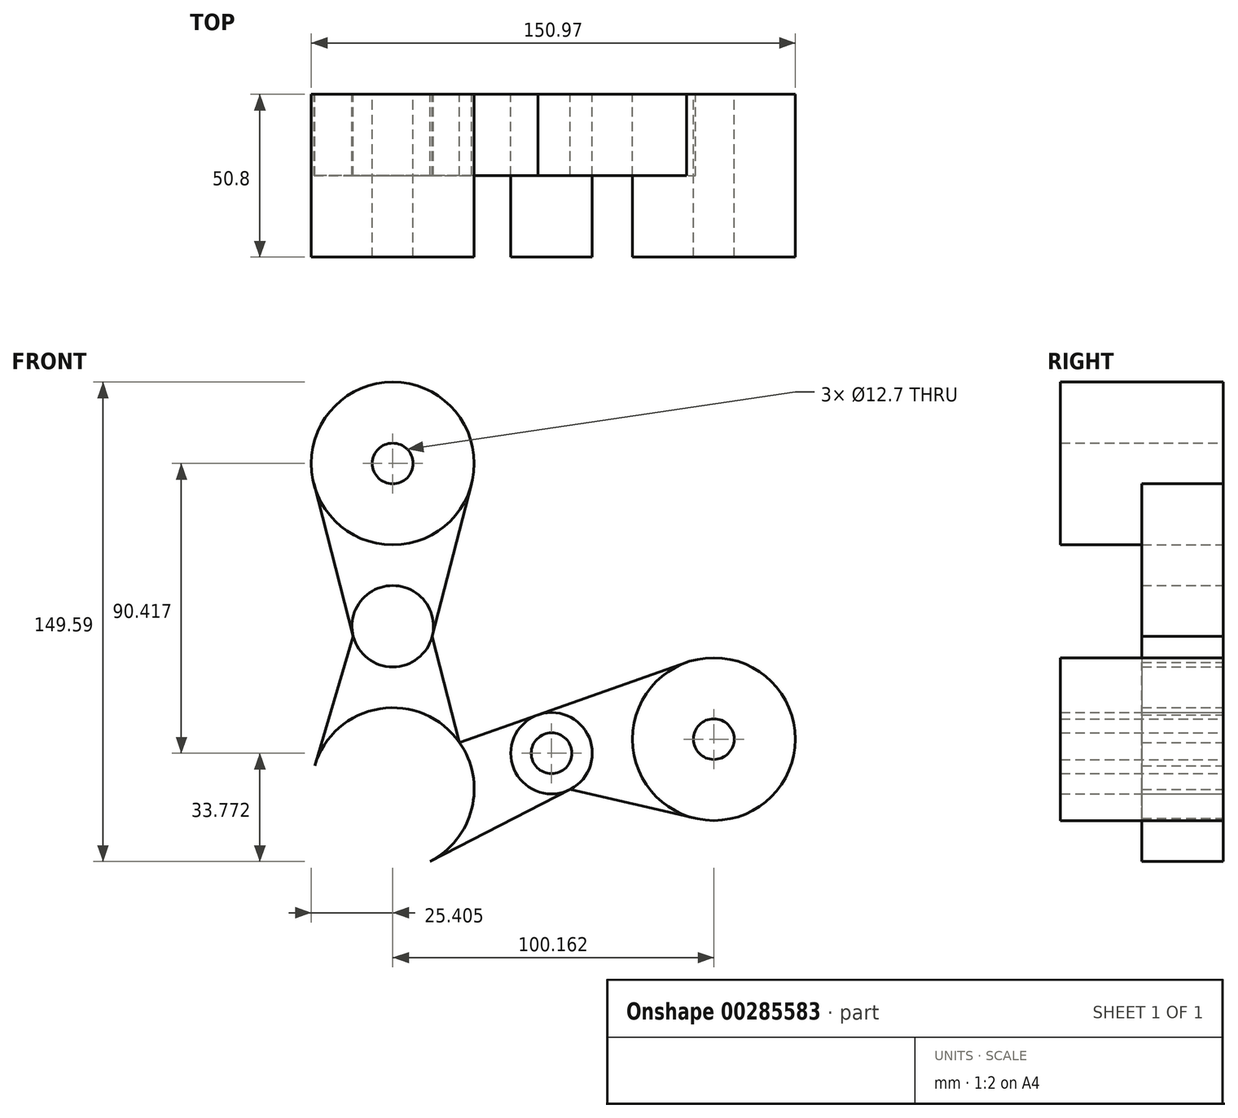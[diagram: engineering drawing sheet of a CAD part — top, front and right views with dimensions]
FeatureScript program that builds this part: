
annotation { "Feature Type Name" : "Feature", "Feature Type Description" : "" }
export const myFeature = defineFeature(function(context is Context, id is Id, definition is map)
    precondition{}
    {
        {
            var Q0;
            Q0=qCreatedBy(makeId("Front.planeOp"),FACE);
            var sketch = newSketch(context, id + "F0", { "sketchPlane" : qUnion([Q0])});
            skLineSegment(sketch, "E0", {"start": v(-250.7, 15.24) * mm, "end": v(-250.7, -86.36) * mm});
            skCircle(sketch, "E1", {"center": v(-250.7, 15.24) * mm, "radius": 25.4 * mm});
            skLineSegment(sketch, "E2", {"start": v(-250.7, 15.24) * mm, "end": v(-250.7, -35.56) * mm});
            skLineSegment(sketch, "E3", {"start": v(-250.7, -35.56) * mm, "end": v(-250.7, -86.36) * mm});
            skLineSegment(sketch, "E4", {"start": v(-201.15, -75.18) * mm, "end": v(-250.7, -86.36) * mm});
            skCircle(sketch, "E5", {"center": v(-250.7, -86.36) * mm, "radius": 25.4 * mm});
            skCircle(sketch, "E6", {"center": v(-150.54, -70.77) * mm, "radius": 25.4 * mm});
            skLineSegment(sketch, "E7", {"start": v(-201.15, -75.18) * mm, "end": v(-150.54, -70.77) * mm});
            skCircle(sketch, "E8", {"center": v(-250.7, -35.56) * mm, "radius": 12.7 * mm});
            skCircle(sketch, "E9", {"center": v(-201.15, -75.18) * mm, "radius": 12.7 * mm});
            skLineSegment(sketch, "E10", {"start": v(-275.3, 8.89) * mm, "end": v(-263, -38.74) * mm});
            skLineSegment(sketch, "E11", {"start": v(-263, -38.74) * mm, "end": v(-275.04, -79.1) * mm});
            skLineSegment(sketch, "E12", {"start": v(-226.11, 8.89) * mm, "end": v(-238.4, -38.74) * mm});
            skLineSegment(sketch, "E13", {"start": v(-205.38, -63.2) * mm, "end": v(-159, -46.82) * mm});
            skLineSegment(sketch, "E14", {"start": v(-238.4, -38.74) * mm, "end": v(-229.86, -71.85) * mm});
            skLineSegment(sketch, "E15", {"start": v(-229.86, -71.85) * mm, "end": v(-205.38, -63.2) * mm});
            skLineSegment(sketch, "E16", {"start": v(-195.35, -86.47) * mm, "end": v(-156.27, -95.52) * mm});
            skLineSegment(sketch, "E17", {"start": v(-239.1, -108.95) * mm, "end": v(-195.35, -86.47) * mm});
            skSolve(sketch);
        }
        {
            var Q0;
            {var subQ0=sQuery(id+"F0.wireOp",EDGE,"E1");var subQ1=makeQuery(id+"F0.imprint","INTERSECT",VERTEX,{"derivedFrom":[subQ0,sQuery(id+"F0.wireOp",EDGE,"E10")]});Q0=makeQuery(id+"F0.imprint","IMPRINT",FACE,{"disambiguationData":[TD([[makeQuery(id+"F0.imprint","IMPRINT",EDGE,{"disambiguationData":[TD([[subQ1,-1.0]])],"derivedFrom":subQ0}),1.0]])]});}
            var Q1;
            {var subQ0=sQuery(id+"F0.wireOp",EDGE,"E3");var subQ1=sQuery(id+"F0.wireOp",EDGE,"E2");var subQ2=makeQuery(id+"F0.imprint","INTERSECT",VERTEX,{"derivedFrom":[subQ1,subQ0]});Q1=makeQuery(id+"F0.imprint","IMPRINT",FACE,{"disambiguationData":[TD([[makeQuery(id+"F0.imprint","IMPRINT",EDGE,{"disambiguationData":[TD([[subQ2,1.0]])],"derivedFrom":subQ1}),1.0]])]});}
            var Q2;
            {var subQ0=sQuery(id+"F0.wireOp",EDGE,"E3");var subQ1=sQuery(id+"F0.wireOp",EDGE,"E2");var subQ2=makeQuery(id+"F0.imprint","INTERSECT",VERTEX,{"derivedFrom":[subQ1,subQ0]});Q2=makeQuery(id+"F0.imprint","IMPRINT",FACE,{"disambiguationData":[TD([[makeQuery(id+"F0.imprint","IMPRINT",EDGE,{"disambiguationData":[TD([[subQ2,1.0]])],"derivedFrom":subQ1}),-1.0]])]});}
            var Q3;
            {var subQ3=sQuery(id+"F0.wireOp",EDGE,"E3");var subQ5=sQuery(id+"F0.wireOp",EDGE,"E4");var subQ6=makeQuery(id+"F0.imprint","INTERSECT",VERTEX,{"derivedFrom":[subQ3,subQ5]});Q3=makeQuery(id+"F0.imprint","IMPRINT",FACE,{"disambiguationData":[TD([[makeQuery(id+"F0.imprint","IMPRINT",EDGE,{"disambiguationData":[TD([[subQ6,1.0]])],"derivedFrom":subQ3}),-1.0]])]});}
            var Q4;
            {var subQ0=sQuery(id+"F0.wireOp",EDGE,"E4");var subQ1=sQuery(id+"F0.wireOp",EDGE,"E3");var subQ2=makeQuery(id+"F0.imprint","INTERSECT",VERTEX,{"derivedFrom":[subQ1,subQ0]});Q4=makeQuery(id+"F0.imprint","IMPRINT",FACE,{"disambiguationData":[TD([[makeQuery(id+"F0.imprint","IMPRINT",EDGE,{"disambiguationData":[TD([[subQ2,1.0]])],"derivedFrom":subQ1}),1.0]])]});}
            var Q5;
            {var subQ0=sQuery(id+"F0.wireOp",EDGE,"E7");var subQ1=sQuery(id+"F0.wireOp",EDGE,"E4");var subQ2=makeQuery(id+"F0.imprint","INTERSECT",VERTEX,{"derivedFrom":[subQ1,subQ0]});Q5=makeQuery(id+"F0.imprint","IMPRINT",FACE,{"disambiguationData":[TD([[makeQuery(id+"F0.imprint","IMPRINT",EDGE,{"disambiguationData":[TD([[subQ2,-1.0]])],"derivedFrom":subQ1}),-1.0]])]});}
            var Q6;
            {var subQ0=sQuery(id+"F0.wireOp",EDGE,"E7");var subQ1=sQuery(id+"F0.wireOp",EDGE,"E4");var subQ2=makeQuery(id+"F0.imprint","INTERSECT",VERTEX,{"derivedFrom":[subQ1,subQ0]});Q6=makeQuery(id+"F0.imprint","IMPRINT",FACE,{"disambiguationData":[TD([[makeQuery(id+"F0.imprint","IMPRINT",EDGE,{"disambiguationData":[TD([[subQ2,-1.0]])],"derivedFrom":subQ1}),1.0]])]});}
            var Q7;
            {var subQ0=sQuery(id+"F0.wireOp",EDGE,"E6");var subQ1=makeQuery(id+"F0.imprint","INTERSECT",VERTEX,{"derivedFrom":[subQ0,sQuery(id+"F0.wireOp",EDGE,"E13")]});Q7=makeQuery(id+"F0.imprint","IMPRINT",FACE,{"disambiguationData":[TD([[makeQuery(id+"F0.imprint","IMPRINT",EDGE,{"disambiguationData":[TD([[subQ1,-1.0]])],"derivedFrom":subQ0}),1.0]])]});}
            extrude(context, id + "F1", {"entities" : qUnion([Q0, Q1, Q2, Q3, Q4, Q5, Q6, Q7]), "depth" : 50.8 * mm});
        }
        {
            var Q0;
            {var subQ0=sQuery(id+"F0.wireOp",EDGE,"E10");Q0=makeQuery(id+"F0.imprint","IMPRINT",FACE,{"disambiguationData":[TD([[makeQuery(id+"F0.imprint","IMPRINT",EDGE,{"derivedFrom":subQ0}),1.0]])]});}
            var Q1;
            {var subQ0=sQuery(id+"F0.wireOp",EDGE,"E12");Q1=makeQuery(id+"F0.imprint","IMPRINT",FACE,{"disambiguationData":[TD([[makeQuery(id+"F0.imprint","IMPRINT",EDGE,{"derivedFrom":subQ0}),-1.0]])]});}
            var Q2;
            {var subQ5=sQuery(id+"F0.wireOp",EDGE,"E14");Q2=makeQuery(id+"F0.imprint","IMPRINT",FACE,{"disambiguationData":[TD([[makeQuery(id+"F0.imprint","IMPRINT",EDGE,{"derivedFrom":subQ5}),-1.0]])]});}
            var Q3;
            {var subQ5=sQuery(id+"F0.wireOp",EDGE,"E11");Q3=makeQuery(id+"F0.imprint","IMPRINT",FACE,{"disambiguationData":[TD([[makeQuery(id+"F0.imprint","IMPRINT",EDGE,{"derivedFrom":subQ5}),1.0]])]});}
            var Q4;
            {var subQ0=sQuery(id+"F0.wireOp",EDGE,"E13");Q4=makeQuery(id+"F0.imprint","IMPRINT",FACE,{"disambiguationData":[TD([[makeQuery(id+"F0.imprint","IMPRINT",EDGE,{"derivedFrom":subQ0}),-1.0]])]});}
            var Q5;
            {var subQ0=sQuery(id+"F0.wireOp",EDGE,"E16");Q5=makeQuery(id+"F0.imprint","IMPRINT",FACE,{"disambiguationData":[TD([[makeQuery(id+"F0.imprint","IMPRINT",EDGE,{"derivedFrom":subQ0}),1.0]])]});}
            var Q6;
            {var subQ5=sQuery(id+"F0.wireOp",EDGE,"E17");Q6=makeQuery(id+"F0.imprint","IMPRINT",FACE,{"disambiguationData":[TD([[makeQuery(id+"F0.imprint","IMPRINT",EDGE,{"derivedFrom":subQ5}),1.0]])]});}
            var Q7;
            {var subQ5=sQuery(id+"F0.wireOp",EDGE,"E15");Q7=makeQuery(id+"F0.imprint","IMPRINT",FACE,{"disambiguationData":[TD([[makeQuery(id+"F0.imprint","IMPRINT",EDGE,{"derivedFrom":subQ5}),-1.0]])]});}
            extrude(context, id + "F2", {"entities" : qUnion([Q0, Q1, Q2, Q3, Q4, Q5, Q6, Q7]), "depth" : 25.4 * mm});
        }
        {
            var Q0;
            Q0=sQuery(id+"F0.wireOp",VERTEX,"E0.start");
            var Q1;
            Q1=sQuery(id+"F0.wireOp",VERTEX,"E3.start");
            var Q2;
            Q2=sQuery(id+"F0.wireOp",VERTEX,"E5.center");
            var Q3;
            Q3=sQuery(id+"F0.wireOp",VERTEX,"E9.center");
            var Q4;
            Q4=sQuery(id+"F0.wireOp",VERTEX,"E7.end");
            var Q5;
            Q5=makeQuery(id+"F1.opExtrude","SWEPT_BODY",BODY,{"disambiguationData":[OSD([sQuery(id+"F0.wireOp",EDGE,"E1")])]});
            var Q6;
            Q6=makeQuery(id+"F1.opExtrude","SWEPT_BODY",BODY,{"disambiguationData":[OSD([sQuery(id+"F0.wireOp",EDGE,"E8")])]});
            var Q7;
            Q7=makeQuery(id+"F1.opExtrude","SWEPT_BODY",BODY,{"disambiguationData":[OSD([sQuery(id+"F0.wireOp",EDGE,"E5")])]});
            var Q8;
            Q8=makeQuery(id+"F1.opExtrude","SWEPT_BODY",BODY,{"disambiguationData":[OSD([sQuery(id+"F0.wireOp",EDGE,"E9")])]});
            var Q9;
            Q9=makeQuery(id+"F1.opExtrude","SWEPT_BODY",BODY,{"disambiguationData":[OSD([sQuery(id+"F0.wireOp",EDGE,"E6")])]});
            hole(context, id + "F3", {"style" : HoleStyle.SIMPLE, "endStyle" : HoleEndStyle.THROUGH, "oppositeDirection" : true, "holeDiameter" : 6.35 * mm, "tappedDepth" : 12.7 * mm, "tapClearance" : 3, "locations" : qUnion([Q0, Q1, Q2, Q3, Q4]), "scope" : qUnion([Q5, Q6, Q7, Q8, Q9])});
        }
        {
            var Q0;
            Q0=sQuery(id+"F0.wireOp",VERTEX,"E0.start");
            var Q1;
            Q1=sQuery(id+"F0.wireOp",VERTEX,"E3.start");
            var Q2;
            Q2=sQuery(id+"F0.wireOp",VERTEX,"E5.center");
            var Q3;
            Q3=sQuery(id+"F0.wireOp",VERTEX,"E9.center");
            var Q4;
            Q4=sQuery(id+"F0.wireOp",VERTEX,"E6.center");
            var Q5;
            Q5=makeQuery(id+"F1.opExtrude","SWEPT_BODY",BODY,{"disambiguationData":[OSD([sQuery(id+"F0.wireOp",EDGE,"E1")])]});
            var Q6;
            Q6=makeQuery(id+"F1.opExtrude","SWEPT_BODY",BODY,{"disambiguationData":[OSD([sQuery(id+"F0.wireOp",EDGE,"E8")])]});
            var Q7;
            Q7=makeQuery(id+"F1.opExtrude","SWEPT_BODY",BODY,{"disambiguationData":[OSD([sQuery(id+"F0.wireOp",EDGE,"E5")])]});
            var Q8;
            Q8=makeQuery(id+"F1.opExtrude","SWEPT_BODY",BODY,{"disambiguationData":[OSD([sQuery(id+"F0.wireOp",EDGE,"E9")])]});
            var Q9;
            Q9=makeQuery(id+"F1.opExtrude","SWEPT_BODY",BODY,{"disambiguationData":[OSD([sQuery(id+"F0.wireOp",EDGE,"E6")])]});
            hole(context, id + "F4", {"style" : HoleStyle.SIMPLE, "endStyle" : HoleEndStyle.THROUGH, "oppositeDirection" : true, "holeDiameter" : 12.7 * mm, "tappedDepth" : 12.7 * mm, "tapClearance" : 3, "locations" : qUnion([Q0, Q1, Q2, Q3, Q4]), "scope" : qUnion([Q5, Q6, Q7, Q8, Q9])});
        }
    });
